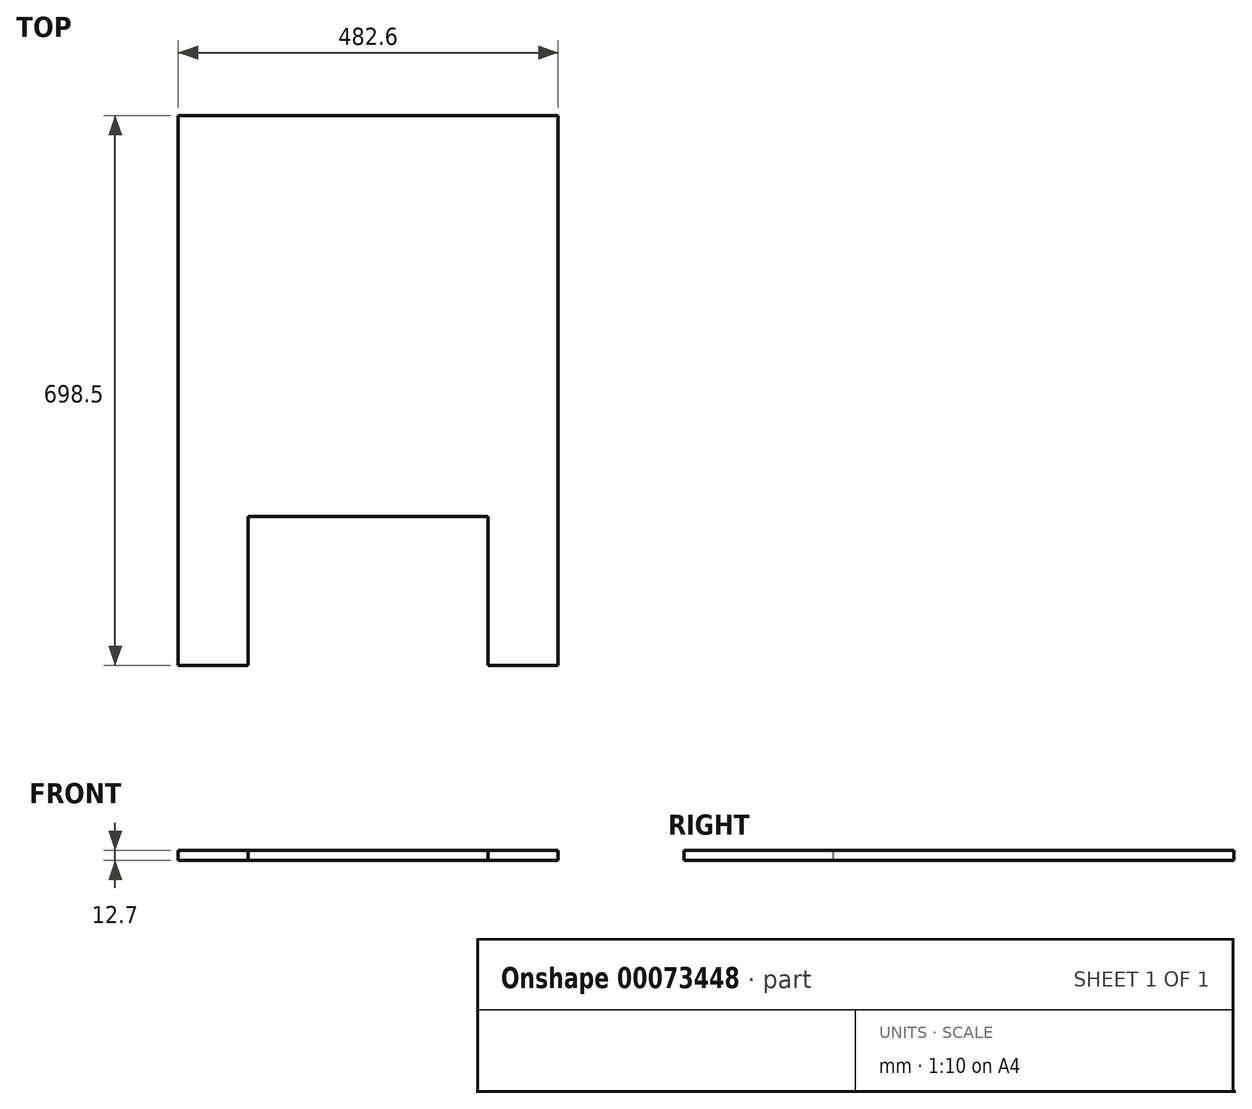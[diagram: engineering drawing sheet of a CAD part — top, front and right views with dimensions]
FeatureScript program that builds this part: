
annotation { "Feature Type Name" : "Feature", "Feature Type Description" : "" }
export const myFeature = defineFeature(function(context is Context, id is Id, definition is map)
    precondition{}
    {
        {
            var Q0;
            Q0=qCreatedBy(makeId("Top.planeOp"),FACE);
            var sketch = newSketch(context, id + "F0", { "sketchPlane" : qUnion([Q0])});
            skLineSegment(sketch, "E0.bottom", {"start": v(-507.16, 268.27) * mm, "end": v(-24.56, 268.27) * mm});
            skLineSegment(sketch, "E0.left", {"start": v(-507.16, 268.27) * mm, "end": v(-507.16, -430.23) * mm});
            skLineSegment(sketch, "E0.right", {"start": v(-24.56, 268.27) * mm, "end": v(-24.56, -430.23) * mm});
            skLineSegment(sketch, "E1", {"start": v(-24.56, -430.23) * mm, "end": v(-113.46, -430.23) * mm});
            skLineSegment(sketch, "E2", {"start": v(-113.46, -430.23) * mm, "end": v(-113.46, -241.24) * mm});
            skLineSegment(sketch, "E3", {"start": v(-113.46, -241.24) * mm, "end": v(-418.26, -241.24) * mm});
            skLineSegment(sketch, "E4", {"start": v(-418.26, -241.24) * mm, "end": v(-418.26, -430.23) * mm});
            skLineSegment(sketch, "E5", {"start": v(-418.26, -430.23) * mm, "end": v(-507.16, -430.23) * mm});
            skSolve(sketch);
        }
        {
            var Q0;
            Q0=makeQuery(id+"F0.imprint","IMPRINT",FACE,{"disambiguationData":[TD([[makeQuery(id+"F0.imprint","IMPRINT",EDGE,{"derivedFrom":sQuery(id+"F0.wireOp",EDGE,"E0.bottom")}),-1.0]])]});
            extrude(context, id + "F1", {"entities" : qUnion([Q0]), "endBound" : BoundingType.SYMMETRIC, "depth" : 12.7 * mm});
        }
    });
